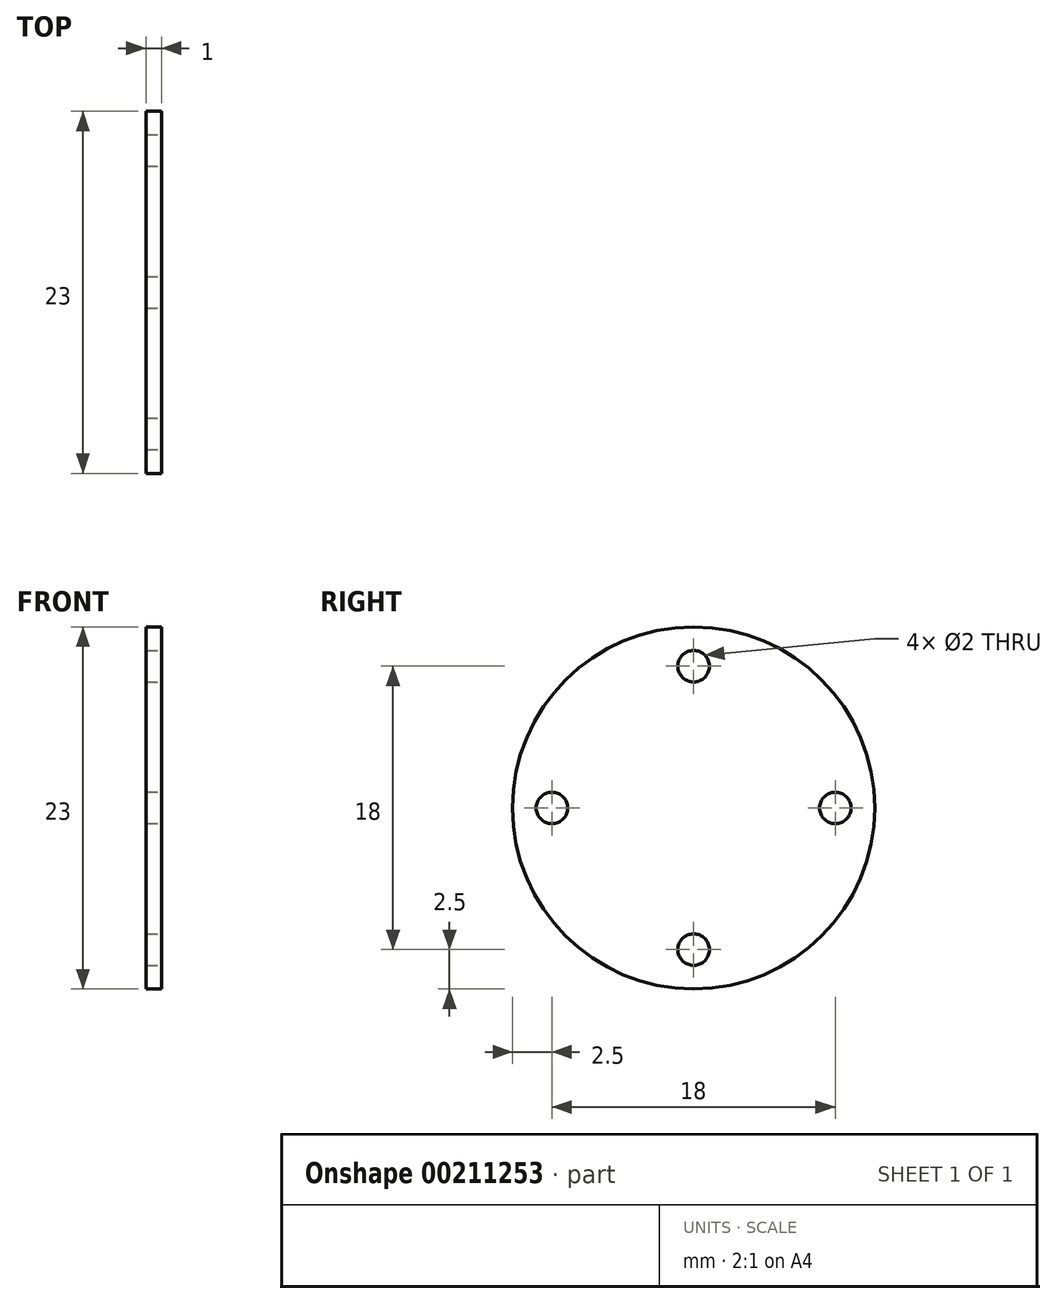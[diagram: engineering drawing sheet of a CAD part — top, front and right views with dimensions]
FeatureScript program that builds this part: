
annotation { "Feature Type Name" : "Feature", "Feature Type Description" : "" }
export const myFeature = defineFeature(function(context is Context, id is Id, definition is map)
    precondition{}
    {
        {
            var Q0;
            Q0=qCreatedBy(makeId("Right.planeOp"),FACE);
            var sketch = newSketch(context, id + "F0", { "sketchPlane" : qUnion([Q0])});
            skCircle(sketch, "E0", {"center": v(0, 0) * mm, "radius": 11.5 * mm});
            skSolve(sketch);
        }
        {
            var Q0;
            Q0 = qSketchRegion(id + "F0", true);
            extrude(context, id + "F1", {"entities" : qUnion([Q0]), "depth" : 1 * mm, "offsetDistance" : 25 * mm});
        }
        {
            var Q0;
            Q0=makeQuery(id+"F1.opExtrude","CAP_FACE",FACE,{"disambiguationData":[OSD([sQuery(id+"F0.wireOp",EDGE,"E0")])],"isStart":false});
            var sketch = newSketch(context, id + "F2", { "sketchPlane" : qUnion([Q0])});
            skCircle(sketch, "E1", {"center": v(0, 0) * mm, "radius": 9 * mm, "construction": true});
            skCircle(sketch, "E2", {"center": v(0, 9) * mm, "radius": 1 * mm});
            skCircle(sketch, "E3", {"center": v(9, 0) * mm, "radius": 1 * mm});
            skCircle(sketch, "E4", {"center": v(0, -9) * mm, "radius": 1 * mm});
            skCircle(sketch, "E5", {"center": v(-9, 0) * mm, "radius": 1 * mm});
            skSolve(sketch);
        }
        {
            var Q0;
            Q0 = qSketchRegion(id + "F2", true);
            extrude(context, id + "F3", {"entities" : qUnion([Q0]), "operationType" : NewBodyOperationType.REMOVE, "endBound" : BoundingType.THROUGH_ALL, "oppositeDirection" : true, "depth" : 25 * mm, "offsetDistance" : 25 * mm});
        }
    });
